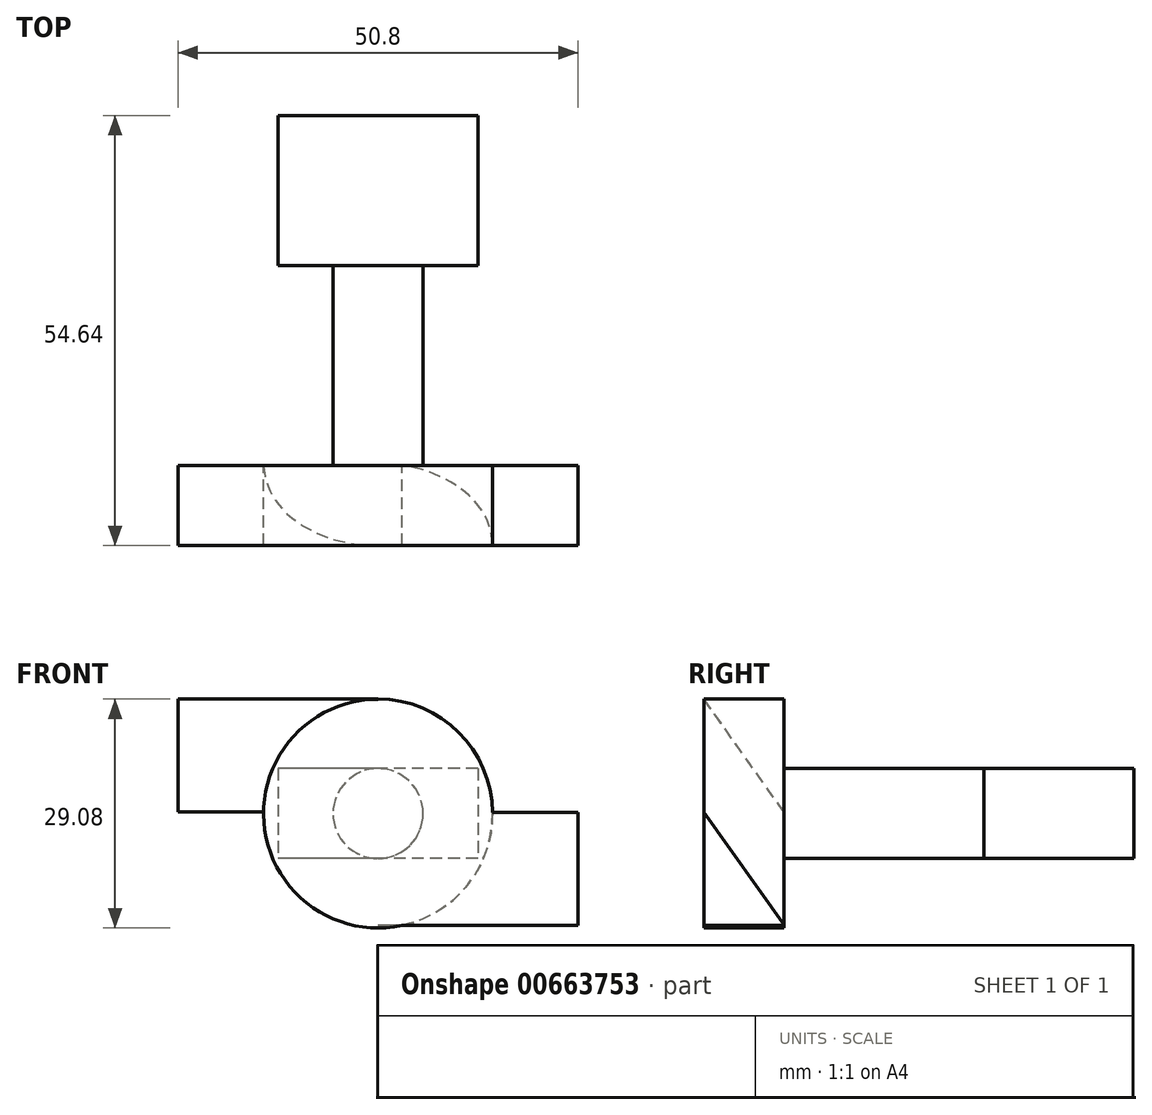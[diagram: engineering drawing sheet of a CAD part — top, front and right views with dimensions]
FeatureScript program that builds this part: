
annotation { "Feature Type Name" : "Feature", "Feature Type Description" : "" }
export const myFeature = defineFeature(function(context is Context, id is Id, definition is map)
    precondition{}
    {
        {
            var Q0;
            Q0=qCreatedBy(makeId("Front.planeOp"),FACE);
            var sketch = newSketch(context, id + "F0", { "sketchPlane" : qUnion([Q0])});
            skCircle(sketch, "E0", {"center": v(0, 0) * mm, "radius": 14.54 * mm});
            skSolve(sketch);
        }
        {
            var Q0;
            Q0 = qSketchRegion(id + "F0", true);
            extrude(context, id + "F1", {"entities" : qUnion([Q0]), "depth" : 10.16 * mm, "offsetDistance" : 25.4 * mm});
        }
        {
            var Q0;
            Q0=qCreatedBy(makeId("Right.planeOp"),FACE);
            var sketch = newSketch(context, id + "F2", { "sketchPlane" : qUnion([Q0])});
            skLineSegment(sketch, "E1", {"start": v(-10.2, 14.54) * mm, "end": v(-0.02, 14.54) * mm});
            skLineSegment(sketch, "E2", {"start": v(-0.02, 14.54) * mm, "end": v(-0.02, 0.18) * mm});
            skLineSegment(sketch, "E3", {"start": v(-0.02, 0.18) * mm, "end": v(-10.2, 14.54) * mm});
            skSolve(sketch);
        }
        {
            var Q0;
            Q0=qCreatedBy(makeId("Right.planeOp"),FACE);
            var sketch = newSketch(context, id + "F3", { "sketchPlane" : qUnion([Q0])});
            skLineSegment(sketch, "E4", {"start": v(0.02, -14.23) * mm, "end": v(-10.16, -14.23) * mm});
            skLineSegment(sketch, "E5", {"start": v(-10.16, -14.23) * mm, "end": v(-10.16, 0.14) * mm});
            skLineSegment(sketch, "E6", {"start": v(-10.16, 0.14) * mm, "end": v(0.02, -14.23) * mm});
            skSolve(sketch);
        }
        {
            var Q0;
            Q0 = qSketchRegion(id + "F3", true);
            extrude(context, id + "F4", {"entities" : qUnion([Q0]), "operationType" : NewBodyOperationType.ADD, "depth" : 25.4 * mm, "offsetDistance" : 25.4 * mm});
        }
        {
            var Q0;
            Q0 = qSketchRegion(id + "F2", true);
            extrude(context, id + "F5", {"entities" : qUnion([Q0]), "operationType" : NewBodyOperationType.ADD, "oppositeDirection" : true, "depth" : 25.4 * mm, "offsetDistance" : 25.4 * mm});
        }
        {
            var Q0;
            Q0=qCreatedBy(makeId("Front.planeOp"),FACE);
            var sketch = newSketch(context, id + "F6", { "sketchPlane" : qUnion([Q0])});
            skCircle(sketch, "E7", {"center": v(0, 0) * mm, "radius": 5.72 * mm});
            skSolve(sketch);
        }
        {
            var Q0;
            Q0 = qSketchRegion(id + "F6", true);
            extrude(context, id + "F7", {"entities" : qUnion([Q0]), "operationType" : NewBodyOperationType.ADD, "oppositeDirection" : true, "depth" : 25.4 * mm, "offsetDistance" : 25.4 * mm});
        }
        {
            var Q0;
            Q0=makeQuery(id+"F7.opExtrude","CAP_FACE",FACE,{"disambiguationData":[OSD([sQuery(id+"F6.wireOp",EDGE,"E7")])],"isStart":false});
            var sketch = newSketch(context, id + "F8", { "sketchPlane" : qUnion([Q0])});
            skLineSegment(sketch, "E8.bottom", {"start": v(-12.7, 5.71) * mm, "end": v(12.7, 5.71) * mm});
            skLineSegment(sketch, "E8.top", {"start": v(-12.7, -5.71) * mm, "end": v(12.7, -5.71) * mm});
            skLineSegment(sketch, "E8.left", {"start": v(-12.7, 5.71) * mm, "end": v(-12.7, -5.71) * mm});
            skLineSegment(sketch, "E8.right", {"start": v(12.7, 5.71) * mm, "end": v(12.7, -5.71) * mm});
            skPoint(sketch, "E8.middle", {"position": v(0, 0) * mm});
            skSolve(sketch);
        }
        {
            var Q0;
            Q0 = qSketchRegion(id + "F8", true);
            extrude(context, id + "F9", {"entities" : qUnion([Q0]), "operationType" : NewBodyOperationType.ADD, "depth" : 19.05 * mm, "offsetDistance" : 25.4 * mm});
        }
    });
